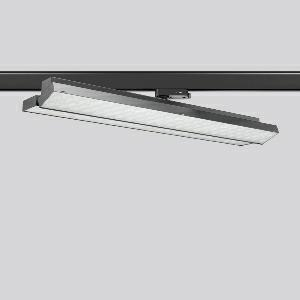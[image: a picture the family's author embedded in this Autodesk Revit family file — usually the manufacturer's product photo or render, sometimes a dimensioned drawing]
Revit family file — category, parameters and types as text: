
# Revit family: tx-move_742163_003_1_9de3
name_source: partatom
category: Lighting Fixtures
units: mm (PartAtom-declared; Revit-internal decimal feet)

## family parameters
Cut with Voids When Loaded = No
Host = Face
Light Source = No
Part Type = Normal
Room Calculation Point = No
Round Connector Dimension = Use Diameter
Shared = No

## types (1)
- MultiLumen 1 (1 x LED Modul 840, 2950 lm, 4000)
    Apparent Load = 41 VA
    CIE Flux Codes = 65 90 98 100 100
    Color Rendering = 80
    Color Temperature = 4000
    Default Elevation = 1800 mm
    Description = Series: TX-MOVE
Multifunctional surface-mounted spotlight for area lighting. Very flat design. Housing: sheet steel, powder-coated. Rotation range: 356°. Swivel range: 90°. Consistent alignment possible with visible tilt scale. High-efficiency LED units with optimum light control thanks to clear plastic (PC) lens optics. Spezielle Mikrostrukturen reduzieren Gelbsaum. Asymmetrical light distribution. With multi adaptor for 3-circuit tracks 230 V. Suitable for Track on ceiling. MultiLumen: Luminous flux adjustable in 3 steps. Factory setting is the highest luminous flux. Environmentally friendly and resource-saving due to replaceable and recyclable components. 
Colour: deep black, matt (RAL 9005)
Length: 570 mm
Width: 119 mm
Height: 92 mm
Lamp: LED
Socket: without socket
Colour temperature: 4000K
Colour rendering index (CRI): 80
System power: 41 W
Rated luminous flux: 5900 lm
Luminous efficiency: 144 lm/W
System power 2: 57 W
Rated luminous flux 2: 8000 lm
Luminous efficiency 2: 140 lm/W
System power 3: 73 W
Rated luminous flux 3: 9750 lm
Luminous efficiency 3: 134 lm/W
Control gear: Regulated power supply
Protection class: I
Type of protection: IP 20
    Height = 75 mm
    Lamp = 1 x LED Modul 840
    Lamp Light Flux = 2950 lm
    Lamp count = 1
    Length = 569 mm
    Lifetime = 50000 h
    Luminous efficacy = 144 lm/W
    Manufacturer = RZB
    ModVariant = No
    Model = 742163.003.1
    Mounting Place = Ceiling
    Mounting Type = Surface mounted
    Number of Poles = 1
    OnlyDefault = Yes
    Power Factor = 1
    Product Name = TX-MOVE
    Product group = Track mounted projectors
    ProductGroupID = 301
    Protection Class = Protection class I
    Protection Degree = IP 20
    RLX_Detail_Level = 1
    RLX_Emergency_Light_Flux = 0 lm
    RLX_Emergency_Type = 0
    RLX_Emergency_Type_DB = No
    RlxData = <blob elided: 57337 chars, md5=ab43210b>
    Socket = socket
    Standby Power = 0 W
    System Light Flux = 5900 lm
    System Power = 41 W
    Type Comments = MultiLumen 1
    Type Image = 742162.003.jpg
    URL = http://relux.com
    VarID = multilumen_1
    Voltage = 0 V
    Weight = 0.00 kg
    Width = 119 mm

## geometry (parser evidence)
native form markers: Blend x4, Sweep x17
no freeform markers — native parametric forms only
